# Revit family: JNRBHSA-All
name_source: partatom
category: Mechanical Equipment
revit_build: Autodesk Revit 2015 (Build: 20160512_1515(x64)
units: mm (PartAtom-declared; Revit-internal decimal feet)

## types (4) — shared parameters
22" Shelf = Yes
Certifications = NSF 7, UL471, CSA
Condensing  Data Volts = 208 V
Condensing Data  Phase = 1
Condensing Frequency (Hz) = 60 (Hz)
DATE = 02/09/2016
DISCHARGE AIR TEMP. = 33 °F
DISCHARGE AIR VELOCITY = 230 FPM
Defrost Num Day = 2
Defrost Termination = 40 °F
Defrost Type = TIMED-OFF DEFROST
Defrosts Per Day_2 = 2
Description = Narrow Reach-In Self-Contained Merchandiser
Discharge Air (°F) = 33°F
Discharge Air Velocity (FPM) = 230 (FPM)
EQUIPMENT DESCRIPTION = Narrow Reach-In Self-Contained Merchandiser
EQUIPMENT MARK = JNRBHSA-PV
GLASS = Glass
Height = 82 1/2"
Item Description = Narrow Reach-In Self-Contained Merchandiser
Legend Number = JNRBHSA-PV
Manufacturer = HILL PHOENIX
Model = JNRBHSA-PV
PAINTED METAL UPPER SHELF = PAINTED SHELVES
Provided Overcurrent Protection = 20
Refrig Charge Lbs = 0
Refrigerant = R404A
Superheat Set Point @ Bulb (°F) = 6-8°
System Data Frequency (Hz) = 60 (Hz)
System Data Phase = 1
System Data Volts = 208 V
Timed-Off Defrost Fail-Safe (Min) = 60 (Min)
Timed-Off Defrost Termination Temp_2 = 40°F
URL = http://www.hillphoenix.com
Width = 34 7/8"
zero-valued in all types: Evap Temp, Load Mbh

## per-type parameters (varying)
| type | 24hr Energy Usage (kWh) | CENTER LINE & DRAIN | Condenser | DOOR CONFIGURATION | Doors/Length | Horsepower | Lbs. of Refrigerant | Length | Locked Rotor (LRA) Amps | NUMBER OF DOORS | Running Load (RLA) Amps |
| 2 Door | 10.3 (kWh) | 30" | 15" | MASTER DOOR : 30" X 68 3/8" 2 DOOR A SWING (LEFT OPENING) | 2 | 1/3 | 2.2 | 60" | 17 A | 2 | 4 A |
| 3 Door | 12.3 (kWh) | 45" | 30" | MASTER DOOR : 30" X 68 3/8" 3 DOOR A SWING (LEFT OPENING) | 3 | 1/3 | 2.6 | 90" | 17 A | 3 | 4 A |
| 4 Door | 13.0 (kWh) | 60" | 45" | MASTER DOOR : 30" X 68 3/8" 4 DOOR A SWING (LEFT OPENING) | 4 | 1/3 | 3.2 | 120" | 29 A | 4 | 6 A |
| 5 Door | 20.1 (kWh) | 75" | 60" | MASTER DOOR : 30" X 68 3/8" 5 DOOR A SWING (LEFT OPENING) | 5 | 1/2 | 3.5 | 150" | 34 A | 5 | 9 A |

## geometry (parser evidence)
native form markers: Blend x14, Sweep x8
no freeform markers — native parametric forms only
